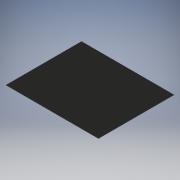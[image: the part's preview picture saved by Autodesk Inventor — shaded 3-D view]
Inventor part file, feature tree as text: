
AUTODESK INVENTOR PART (.ipt)
format: ipt  version: 2016 (Build 200138000, 138)  size: 100,864 bytes
history: native  units: mm
features: extrude x1, sketch x1
ambient origin geometry x8: Origin, YZ Plane, XZ Plane, XY Plane, X Axis, Y Axis, Z Axis, Center Point
bodies: Body1 (feature_tree)
feature tree (2):
  extrude  "押し出し5"  Depth=14.5mm
  sketch  "スケッチ1"
